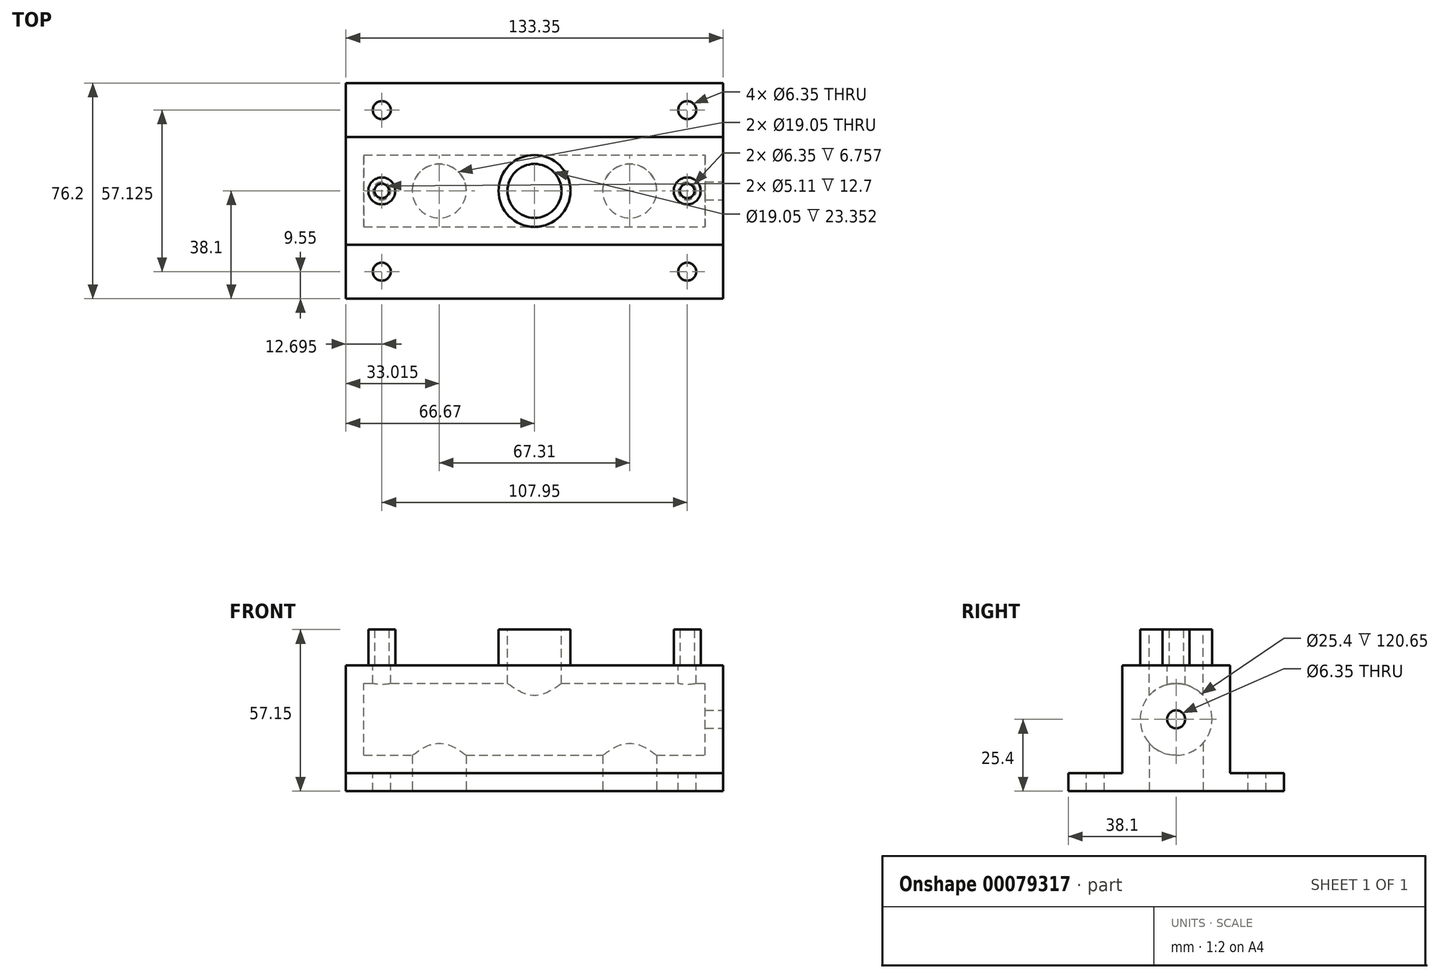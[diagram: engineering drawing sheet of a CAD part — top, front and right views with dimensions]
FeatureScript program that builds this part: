
annotation { "Feature Type Name" : "Feature", "Feature Type Description" : "" }
export const myFeature = defineFeature(function(context is Context, id is Id, definition is map)
    precondition{}
    {
        {
            var Q0;
            Q0=qCreatedBy(makeId("Right.planeOp"),FACE);
            var sketch = newSketch(context, id + "F0", { "sketchPlane" : qUnion([Q0])});
            skLineSegment(sketch, "E0.bottom", {"start": v(-19.05, 19.05) * mm, "end": v(19.05, 19.05) * mm});
            skLineSegment(sketch, "E0.top", {"start": v(-19.05, -19.05) * mm, "end": v(19.05, -19.05) * mm});
            skLineSegment(sketch, "E0.left", {"start": v(-19.05, 19.05) * mm, "end": v(-19.05, -19.05) * mm});
            skLineSegment(sketch, "E0.right", {"start": v(19.05, 19.05) * mm, "end": v(19.05, -19.05) * mm});
            skPoint(sketch, "E0.middle", {"position": v(0, 0) * mm});
            skSolve(sketch);
        }
        {
            var Q0;
            Q0 = qSketchRegion(id + "F0", true);
            extrude(context, id + "F1", {"entities" : qUnion([Q0]), "endBound" : BoundingType.SYMMETRIC, "depth" : 133.35 * mm});
        }
        {
            var Q0;
            Q0=makeQuery(id+"F1.opExtrude","CAP_FACE",FACE,{"disambiguationData":[OSD([sQuery(id+"F0.wireOp",EDGE,"E0.bottom"),sQuery(id+"F0.wireOp",EDGE,"E0.top"),sQuery(id+"F0.wireOp",EDGE,"E0.left"),sQuery(id+"F0.wireOp",EDGE,"E0.right")])],"isStart":false});
            cPlane(context, id + "F2", {"entities" : qUnion([Q0]), "cplaneType" : CPlaneType.OFFSET, "offset" : 6.35 * mm, "oppositeDirection" : true, "width" : 152.4 * mm, "height" : 152.4 * mm});
        }
        {
            var Q0;
            Q0=qCreatedBy(id+"F2.planeOp",FACE);
            var sketch = newSketch(context, id + "F3", { "sketchPlane" : qUnion([Q0])});
            skCircle(sketch, "E1", {"center": v(0, 0) * mm, "radius": 12.7 * mm});
            skSolve(sketch);
        }
        {
            var Q0;
            Q0 = qSketchRegion(id + "F3", true);
            extrude(context, id + "F4", {"entities" : qUnion([Q0]), "operationType" : NewBodyOperationType.REMOVE, "oppositeDirection" : true, "depth" : 120.65 * mm});
        }
        {
            var Q0;
            Q0=makeQuery(id+"F1.opExtrude","SWEPT_FACE",FACE,{"disambiguationData":[OSD([sQuery(id+"F0.wireOp",EDGE,"E0.top")])]});
            var sketch = newSketch(context, id + "F5", { "sketchPlane" : qUnion([Q0])});
            skLineSegment(sketch, "E2.bottom", {"start": v(-66.68, 38.1) * mm, "end": v(66.68, 38.1) * mm});
            skLineSegment(sketch, "E2.top", {"start": v(-66.68, -38.1) * mm, "end": v(66.68, -38.1) * mm});
            skLineSegment(sketch, "E2.left", {"start": v(-66.68, 38.1) * mm, "end": v(-66.68, -38.1) * mm});
            skLineSegment(sketch, "E2.right", {"start": v(66.68, 38.1) * mm, "end": v(66.68, -38.1) * mm});
            skPoint(sketch, "E2.middle", {"position": v(0, 0) * mm});
            skCircle(sketch, "E3", {"center": v(-53.98, 28.55) * mm, "radius": 3.18 * mm});
            skCircle(sketch, "E4", {"center": v(53.98, 28.55) * mm, "radius": 3.18 * mm});
            skCircle(sketch, "E5", {"center": v(53.98, -28.58) * mm, "radius": 3.18 * mm});
            skCircle(sketch, "E6", {"center": v(-53.98, -28.58) * mm, "radius": 3.18 * mm});
            skSolve(sketch);
        }
        {
            var Q0;
            Q0 = qSketchRegion(id + "F5", true);
            extrude(context, id + "F6", {"entities" : qUnion([Q0]), "operationType" : NewBodyOperationType.ADD, "depth" : 6.35 * mm});
        }
        {
            var Q0;
            Q0=makeQuery(id+"F6.opExtrude","CAP_FACE",FACE,{"disambiguationData":[OSD([sQuery(id+"F5.wireOp",EDGE,"E2.bottom"),sQuery(id+"F5.wireOp",EDGE,"E2.top"),sQuery(id+"F5.wireOp",EDGE,"E2.left"),sQuery(id+"F5.wireOp",EDGE,"E2.right"),sQuery(id+"F5.wireOp",EDGE,"E3"),sQuery(id+"F5.wireOp",EDGE,"E4"),sQuery(id+"F5.wireOp",EDGE,"E5"),sQuery(id+"F5.wireOp",EDGE,"E6")])],"isStart":false});
            var sketch = newSketch(context, id + "F7", { "sketchPlane" : qUnion([Q0])});
            skLineSegment(sketch, "E7", {"start": v(-47.1, 0) * mm, "end": v(45.83, 0) * mm, "construction": true});
            skPoint(sketch, "E7.endSnap0", {"position": v(66.68, 0) * mm});
            skCircle(sketch, "E8", {"center": v(-33.66, 0) * mm, "radius": 9.53 * mm});
            skCircle(sketch, "E9", {"center": v(33.66, 0) * mm, "radius": 9.53 * mm});
            skSolve(sketch);
        }
        {
            var Q0;
            Q0 = qSketchRegion(id + "F7", true);
            extrude(context, id + "F8", {"entities" : qUnion([Q0]), "operationType" : NewBodyOperationType.REMOVE, "oppositeDirection" : true, "depth" : 25.4 * mm});
        }
        {
            var Q0;
            Q0=makeQuery(id+"F1.opExtrude","SWEPT_FACE",FACE,{"disambiguationData":[OSD([sQuery(id+"F0.wireOp",EDGE,"E0.bottom")])]});
            var sketch = newSketch(context, id + "F9", { "sketchPlane" : qUnion([Q0])});
            skCircle(sketch, "E10", {"center": v(0, 0) * mm, "radius": 9.53 * mm});
            skCircle(sketch, "E11", {"center": v(-53.98, 0) * mm, "radius": 3.18 * mm});
            skCircle(sketch, "E12", {"center": v(53.98, 0) * mm, "radius": 3.18 * mm});
            skSolve(sketch);
        }
        {
            var Q0;
            Q0 = qSketchRegion(id + "F9", true);
            extrude(context, id + "F10", {"entities" : qUnion([Q0]), "operationType" : NewBodyOperationType.REMOVE, "oppositeDirection" : true, "depth" : 19.05 * mm});
        }
        {
            var Q0;
            Q0=makeQuery(id+"F1.opExtrude","SWEPT_FACE",FACE,{"disambiguationData":[OSD([sQuery(id+"F0.wireOp",EDGE,"E0.bottom")])]});
            var sketch = newSketch(context, id + "F11", { "sketchPlane" : qUnion([Q0])});
            skCircle(sketch, "E13", {"center": v(-53.98, 0) * mm, "radius": 4.76 * mm});
            skCircle(sketch, "E14", {"center": v(-53.98, 0) * mm, "radius": 2.55 * mm});
            skCircle(sketch, "E15", {"center": v(0, 0) * mm, "radius": 9.53 * mm});
            skCircle(sketch, "E16", {"center": v(0, 0) * mm, "radius": 12.7 * mm});
            skCircle(sketch, "E17", {"center": v(53.98, 0) * mm, "radius": 2.55 * mm});
            skCircle(sketch, "E18", {"center": v(53.98, 0) * mm, "radius": 4.76 * mm});
            skSolve(sketch);
        }
        {
            var Q0;
            Q0 = qSketchRegion(id + "F11", true);
            extrude(context, id + "F12", {"entities" : qUnion([Q0]), "operationType" : NewBodyOperationType.ADD, "depth" : 12.7 * mm});
        }
        {
            var Q0;
            Q0=makeQuery(id+"F6.boolean.opBoolean","MERGE",FACE,{"derivedFrom":[makeQuery(id+"F1.opExtrude","CAP_FACE",FACE,{"disambiguationData":[OSD([sQuery(id+"F0.wireOp",EDGE,"E0.bottom"),sQuery(id+"F0.wireOp",EDGE,"E0.top"),sQuery(id+"F0.wireOp",EDGE,"E0.left"),sQuery(id+"F0.wireOp",EDGE,"E0.right")])],"isStart":false}),makeQuery(id+"F6.opExtrude","SWEPT_FACE",FACE,{"disambiguationData":[OSD([sQuery(id+"F5.wireOp",EDGE,"E2.right")])]})]});
            var sketch = newSketch(context, id + "F13", { "sketchPlane" : qUnion([Q0])});
            skCircle(sketch, "E19", {"center": v(0, 0) * mm, "radius": 3.18 * mm});
            skSolve(sketch);
        }
        {
            var Q0;
            Q0 = qSketchRegion(id + "F13", true);
            extrude(context, id + "F14", {"entities" : qUnion([Q0]), "operationType" : NewBodyOperationType.REMOVE, "oppositeDirection" : true, "depth" : 12.7 * mm});
        }
    });
